# Revit family: 797fd971-885e-4052-8578-c5b3330441d4
name_source: partatom
category: Двери
revit_build: Autodesk Revit 2017 (Build: 20170419_0315(x64)
units: mm (PartAtom-declared; Revit-internal decimal feet)

## family parameters
Всегда вертикально = Да
Заголовок OmniClass = Doors
Номер OmniClass = 23.30.10.00
Общий = Нет
Основа = Стена
При загрузке вырезать с полостями = Нет
Точка расчета площади = Нет

## types (1)
- 797fd971-885e-4052-8578-c5b3330441d4
    00_СмещениеОтСтены = 15 мм
    00_ШиринаКоробки = 5 мм
    00_ШиринаМонтажногоЗазора = 10 мм
    a = 913 мм
    b = 2000 мм
    c = 3805 мм
    Аналитическая конструкция = <Нет>
    Высота = 2100 мм
    Выступ каркаса внут. = 25 мм
    Выступ каркаса нар. = 25 мм
    ДопРазмер = 205 мм
    Замыкание стены = По основе
    МатериалКоробки = <По категории>
    МатериалПрофилей = <По категории>
    МатериалРучки = <По категории>
    МатериалСтекла = Стекло
    О_Масса = 0
    Примерная высота = 2100 мм
    Примерная ширина = 1800 мм
    Р_Высота = 2100 мм
    Р_Ширина = 1800 мм
    Функция = Внутренние слои
    Ширина = 1800 мм
    Ширина каркаса = 75 мм
